# Revit family: Diverter-2_Way-Two_Handle-Grohe-Lineare-29421_Series
name_source: partatom
category: Plumbing Fixtures
units: mm (PartAtom-declared; Revit-internal decimal feet)

## family parameters
Cut with Voids When Loaded = No
Host = Face
OmniClass Number = 23.65.55.14
OmniClass Title = Valves for Liquid Services
Part Type = Normal
Room Calculation Point = No
Round Connector Dimension = Use Diameter
Shared = Yes

## types (4) — shared parameters
35117000 GROHSAFE 3.0 PRESSURE BALANCE VALVE WITH INTEGRATED DIVERTER = No
ADA Compliant = Yes
ASME A112.18.1/CSA B125.1/ASSE 1016 = Yes
Assembly Code = D2020300
CEC Compliant = Yes
CW Connection = Yes
CWFU = 3
Cold Water Connection Diameter = 1/2"
Compliance Certifications = • ADA• CEC Certified• CALGreen Compliant• Massachusetts Plumbing Board Approved• ASSE 1016• CSA B125.1• CSA B125.16• ASME A112.18.1• ASME A112.1016
Default Elevation = 48"
Description = LINEARE PRESSURE BALANCE VALVE TRIM WITH 2-WAY DIVERTER WITH CARTRIDGE
Diameter = 7 3/4"
HW Connection = Yes
HWFU = 3
Height = 9 1/2"
Hot Water Connection Diameter = 1"
Installation Type = Wall Mounted
Length = 2 3/4"
Manufacturer = GROHE
Price = Prices may vary. Please consult Manufacturer Representative for most up-to-date price list.
Product Documentation Link = https://americanstandard.box.com
Product Page URL = https://www.grohe.us
Revised Date = 06/01/2023
Tempered Water Connection = Yes
Tempered Water Connection Diameter = 1/2"
URL = https://www.grohe.us
Vent Connection = No
WFU = 4
Waste Connection = No

## per-type parameters (varying)
| type | Finish | Material |
| 29421000 | Metal-Grohe-000-StarLight Chrome | Metal-Grohe-000-StarLight Chrome |
| 29421A00 | Metal-Grohe-A00-Hard Graphite | Metal-Grohe-A00-Hard Graphite |
| 29421EN0 | Metal-Grohe-EN0-Brushed Nickel | Metal-Grohe-EN0-Brushed Nickel |
| 29421GN0 | Metal-Grohe-GN0-Brushed Cool Sunrise | Metal-Grohe-GN0-Brushed Cool Sunrise |

note: column(s) folded — value = type name in every type: Model

## geometry (parser evidence)
native form markers: Sweep x3
no freeform markers — native parametric forms only
